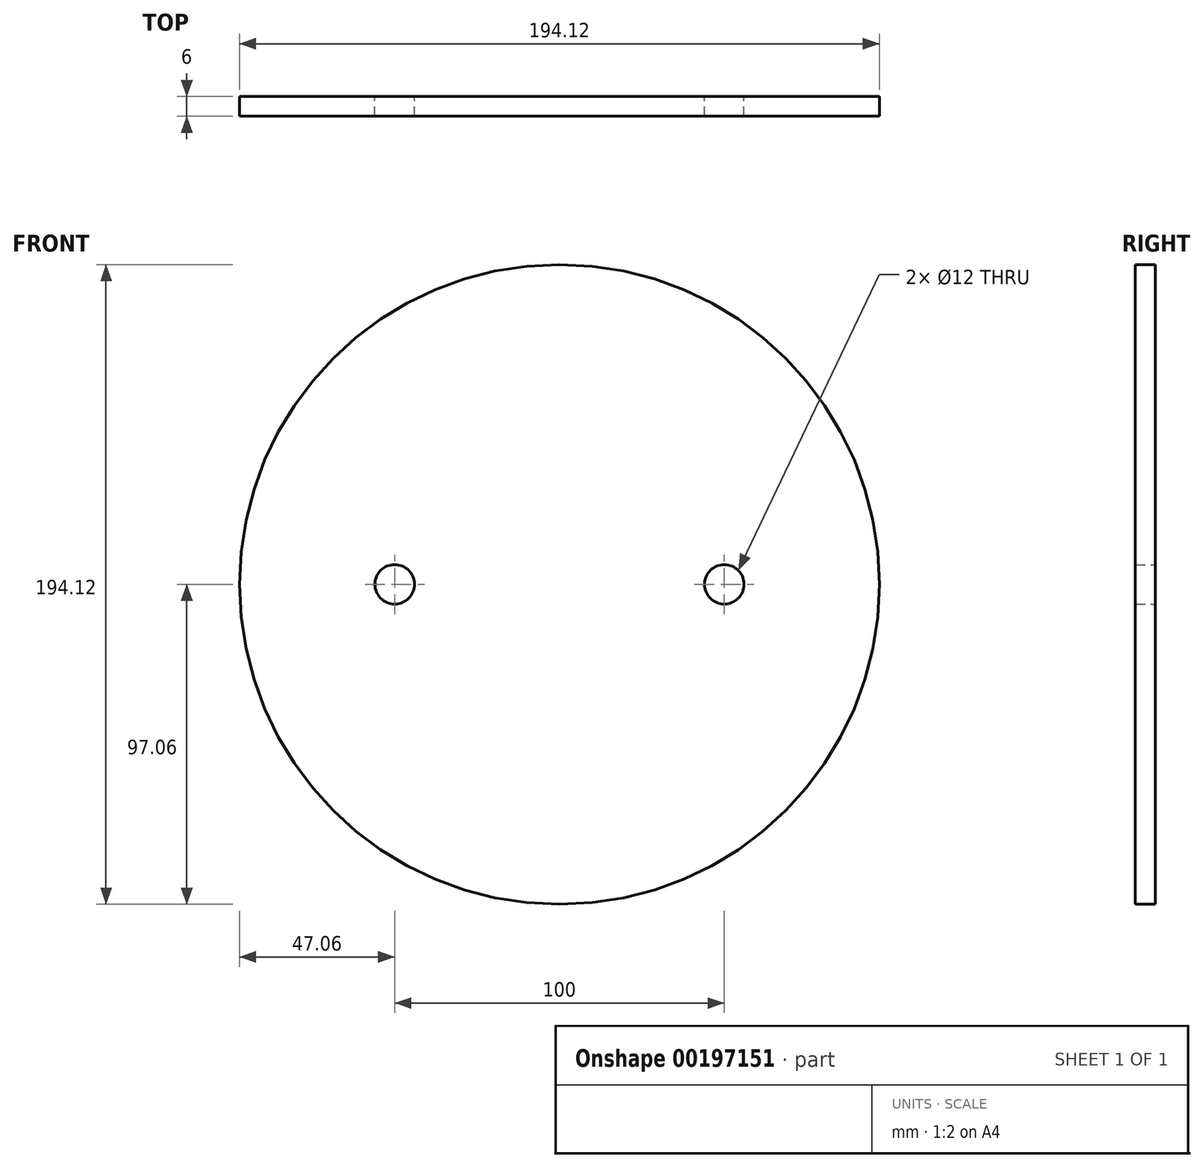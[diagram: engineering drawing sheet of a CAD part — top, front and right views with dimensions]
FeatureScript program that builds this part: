
annotation { "Feature Type Name" : "Feature", "Feature Type Description" : "" }
export const myFeature = defineFeature(function(context is Context, id is Id, definition is map)
    precondition{}
    {
        {
            var Q0;
            Q0=qCreatedBy(makeId("Front.planeOp"),FACE);
            var sketch = newSketch(context, id + "F0", { "sketchPlane" : qUnion([Q0])});
            skCircle(sketch, "E0", {"center": v(0, 0) * mm, "radius": 97.06 * mm});
            skLineSegment(sketch, "E1", {"start": v(0, 0) * mm, "end": v(50, 0) * mm, "construction": true});
            skCircle(sketch, "E2", {"center": v(50, 0) * mm, "radius": 6 * mm});
            skCircle(sketch, "E3", {"center": v(-50, 0) * mm, "radius": 6 * mm});
            skSolve(sketch);
        }
        {
            var Q0;
            Q0 = qSketchRegion(id + "F0", true);
            extrude(context, id + "F1", {"entities" : qUnion([Q0]), "depth" : 6 * mm});
        }
    });
